# Revit family: Domotics-DomesticRanges-GEWISS-CHORUS_COMMAND-BLANKING_MODULE_HOLED
name_source: partatom
category: Apparecchi elettrici
revit_build: Autodesk Revit 2016 (Build: 20161004_0715(x64)
units: mm (PartAtom-declared; Revit-internal decimal feet)

## family parameters
Condiviso = Sì
Host = Superficie
Mantenere orientamento annotazione = Sì
Punto di calcolo locali = Sì
Quota connettore circolare = Usa diametro
Taglio con vuoti quando caricato = Sì
Tipo di parte = Normale

## types (6) — shared parameters
Altezza_copriforo = 45 mm  [stored 0.147638 ft]
Bidimensionale = bidimensionale copriforo bidimensionale : Simbolo bidimensionle
Catalogue = DOMOTICS
Catalogue Range = CHORUS - DOMESTIC RANGE
Category = Blanking module with cable output
Electrocod = 0100
Glow Wire Test = 850°C
IDF = 1e4789e5-7b2b-463d-b32f-6fcb8ce46c3b
IDT = 8a8f33ae-4355-4f43-b13f-60670ae3a502
Larghezza copriforo = 23 mm  [stored 0.0754593 ft]
Produttore = GEWISS S.p.A.
Prospetto di default = 1219 mm
SEO = Cable outlet
Standard = EN 60669-1
Standard; = EN 60669-1
Technical sheet = https://www.gewiss.com
Thermo-pressure with ball = 125
Tipo_ = CHORUS COPRIFORO_generico : GW14195 Copriforo 1M titanio
URL = https://www.gewiss.com
Version file RFA = 19.0

## per-type parameters (varying)
| type | Colour | Description: | Descrizione | EAN code | Modello | No. Chorus modules |
| GW10196 - Blanking module 1M cable output white | White | 1 gang | BLANKING MODULE 1M CABLE OUTPUT WHITE | 8011564258945 | GW10196 | 1 |
| GW12196 - Blanking module 1M cable output black | Black | 1 gang | BLANKING MODULE, 1M, CABLE OUTPUT, BLACK | 8011564266636 | GW12196 | 1 |
| GW14194 - Blanking module 2M cable output titanium | Titanium | 2 gang | BLANKING MODULE 2M CABLE OUTPUT TITANIUM | 8011564298828 | GW14194 | 2 |
| GW14196 - Blanking module 1M cable output titanium | Titanium | 1 gang | BLANKING MODULE, 1M, CABLE OUTPUT T | 8011564266254 | GW14196 | 1 |
| GW12194 - Blanking module 2M cable output black | Black | 2 gang | BLANKING MODULE 2M CABLE OUTPUT BLACK | 8011564298811 | GW12194 | 2 |
| GW10194 - Blanking module 2M cable output white | White | 2 gang | BLANKING MODULE 2M CABLE OUTPUT WHITE | 8011564298804 | GW10194 | 2 |

note: source unit labels omitted for Thermo-pressure with ball — the stored unit's dimension contradicts the parameter name (converter mislabeling)

note: [stored X ft] marks values corroborated as IEEE doubles in the binary element streams (Revit-internal decimal feet)

## geometry (parser evidence)
native form markers: Sweep x6
no freeform markers — native parametric forms only
